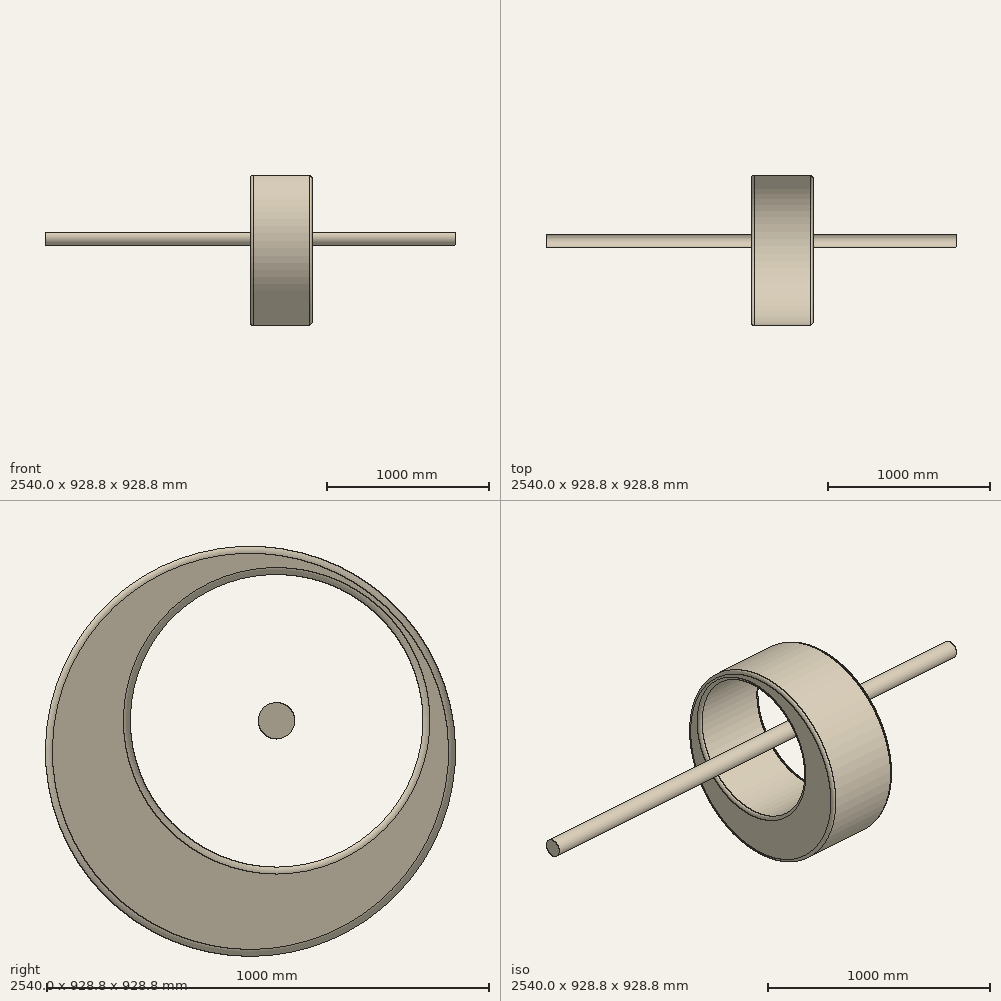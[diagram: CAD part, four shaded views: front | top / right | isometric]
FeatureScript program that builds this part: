
annotation { "Feature Type Name" : "Feature", "Feature Type Description" : "" }
export const myFeature = defineFeature(function(context is Context, id is Id, definition is map)
    precondition{}
    {
        {
            var Q0;
            Q0=qCreatedBy(makeId("Right.planeOp"),FACE);
            var sketch = newSketch(context, id + "F0", { "sketchPlane" : qUnion([Q0])});
            skCircle(sketch, "E0", {"center": v(0, 0) * mm, "radius": 331.3 * mm});
            skCircle(sketch, "E1", {"center": v(-59.25, -69.2) * mm, "radius": 464.38 * mm});
            skSolve(sketch);
        }
        {
            var Q0;
            Q0=makeQuery(id+"F0.imprint","IMPRINT",FACE,{"disambiguationData":[TD([[makeQuery(id+"F0.imprint","IMPRINT",EDGE,{"derivedFrom":sQuery(id+"F0.wireOp",EDGE,"E0")}),-1.0]])]});
            extrude(context, id + "F1", {"entities" : qUnion([Q0]), "depth" : 381.38 * mm, "offsetDistance" : 25.4 * mm});
        }
        {
            var Q0;
            Q0=makeQuery(id+"F1.opExtrude","CAP_EDGE",EDGE,{"disambiguationData":[OSD([sQuery(id+"F0.wireOp",EDGE,"E1")])],"isStart":false});
            var Q1;
            Q1=makeQuery(id+"F1.opExtrude","CAP_EDGE",EDGE,{"disambiguationData":[OSD([sQuery(id+"F0.wireOp",EDGE,"E0")])],"isStart":false});
            fillet(context, id + "F2", {"entities" : qUnion([Q0, Q1]), "radius" : 15.75 * mm, "tangentPropagation" : true, "allowEdgeOverflow" : false});
        }
        {
            var Q0;
            Q0=makeQuery(id+"F1.opExtrude","CAP_EDGE",EDGE,{"disambiguationData":[OSD([sQuery(id+"F0.wireOp",EDGE,"E1")])],"isStart":true});
            var Q1;
            Q1=makeQuery(id+"F1.opExtrude","CAP_EDGE",EDGE,{"disambiguationData":[OSD([sQuery(id+"F0.wireOp",EDGE,"E0")])],"isStart":true});
            fillet(context, id + "F3", {"entities" : qUnion([Q0, Q1]), "radius" : 15.88 * mm, "tangentPropagation" : true, "allowEdgeOverflow" : false});
        }
        {
            var Q0;
            Q0 = qSketchRegion(id + "F0", true);
            var sketch = newSketch(context, id + "F4", { "sketchPlane" : qUnion([Q0])});
            skCircle(sketch, "E2", {"center": v(0, 0) * mm, "radius": 41.24 * mm});
            skSolve(sketch);
        }
        {
            var Q0;
            Q0 = qSketchRegion(id + "F4", true);
            extrude(context, id + "F5", {"entities" : qUnion([Q0]), "endBound" : BoundingType.SYMMETRIC, "depth" : 2540 * mm, "offsetDistance" : 25.4 * mm});
        }
    });
